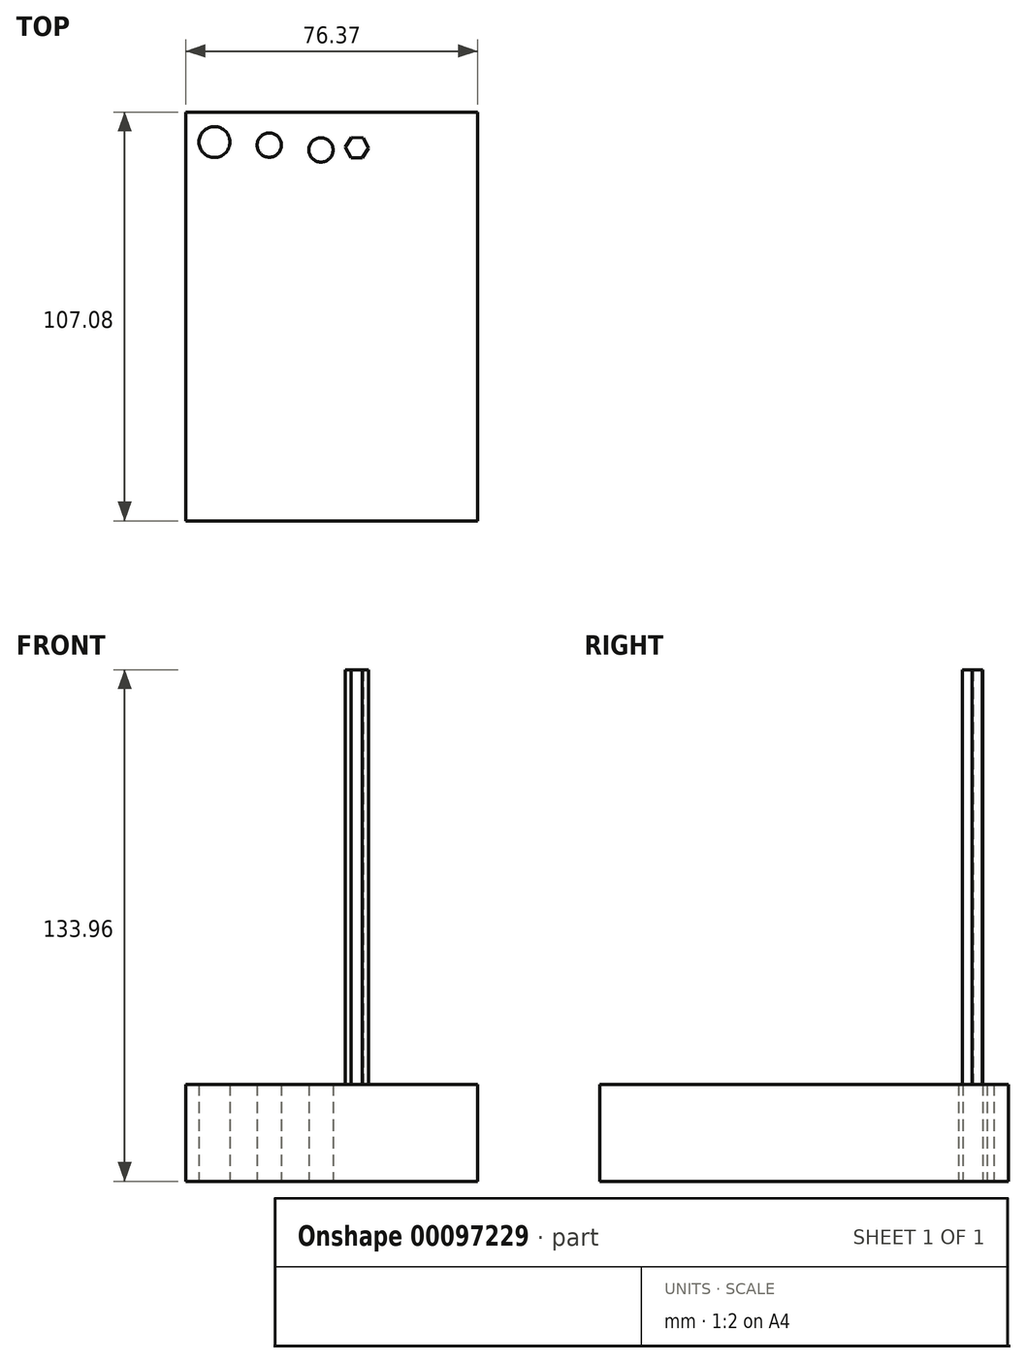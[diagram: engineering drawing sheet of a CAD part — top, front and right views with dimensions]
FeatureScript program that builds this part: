
annotation { "Feature Type Name" : "Feature", "Feature Type Description" : "" }
export const myFeature = defineFeature(function(context is Context, id is Id, definition is map)
    precondition{}
    {
        {
            var Q0;
            Q0=qCreatedBy(makeId("Top.planeOp"),FACE);
            var sketch = newSketch(context, id + "F0", { "sketchPlane" : qUnion([Q0])});
            skLineSegment(sketch, "E0.bottom", {"start": v(-56.88, 53.44) * mm, "end": v(19.49, 53.44) * mm});
            skLineSegment(sketch, "E0.top", {"start": v(-56.88, -53.64) * mm, "end": v(19.49, -53.64) * mm});
            skLineSegment(sketch, "E0.left", {"start": v(-56.88, 53.44) * mm, "end": v(-56.88, -53.64) * mm});
            skLineSegment(sketch, "E0.right", {"start": v(19.49, 53.44) * mm, "end": v(19.49, -53.64) * mm});
            skCircle(sketch, "E1", {"center": v(-49.4, 45.57) * mm, "radius": 4.05 * mm});
            skSolve(sketch);
        }
        {
            var Q0;
            Q0=makeQuery(id+"F0.imprint","IMPRINT",FACE,{"disambiguationData":[TD([[makeQuery(id+"F0.imprint","IMPRINT",EDGE,{"derivedFrom":sQuery(id+"F0.wireOp",EDGE,"E0.bottom")}),-1.0]])]});
            extrude(context, id + "F1", {"entities" : qUnion([Q0]), "depth" : 25.4 * mm});
        }
        {
            var Q0;
            Q0=qCreatedBy(makeId("Top.planeOp"),FACE);
            var sketch = newSketch(context, id + "F2", { "sketchPlane" : qUnion([Q0])});
            skCircle(sketch, "E2", {"center": v(-35.04, 44.78) * mm, "radius": 3.8 * mm});
            skSolve(sketch);
        }
        {
            var Q0;
            Q0=sQuery(id+"F2.wireOp",VERTEX,"E2.center");
            var Q1;
            Q1=makeQuery(id+"F1.opExtrude","SWEPT_BODY",BODY,{"disambiguationData":[OSD([sQuery(id+"F0.wireOp",EDGE,"E0.bottom"),sQuery(id+"F0.wireOp",EDGE,"E0.top"),sQuery(id+"F0.wireOp",EDGE,"E0.left"),sQuery(id+"F0.wireOp",EDGE,"E0.right"),sQuery(id+"F0.wireOp",EDGE,"E1")])]});
            hole(context, id + "F3", {"style" : HoleStyle.SIMPLE, "endStyle" : HoleEndStyle.THROUGH, "oppositeDirection" : true, "holeDiameter" : 6.35 * mm, "locations" : qUnion([Q0]), "scope" : qUnion([Q1]), "isTappedThrough" : true});
        }
        {
            var Q0;
            Q0=qCreatedBy(makeId("Top.planeOp"),FACE);
            var sketch = newSketch(context, id + "F4", { "sketchPlane" : qUnion([Q0])});
            skCircle(sketch, "E3.cCircle", {"center": v(-22.06, 45.19) * mm, "radius": 3.34 * mm, "construction": true});
            skLineSegment(sketch, "E3.0", {"start": v(-20.13, 41.85) * mm, "end": v(-23.99, 41.85) * mm});
            skLineSegment(sketch, "E3.1", {"start": v(-23.99, 41.85) * mm, "end": v(-25.91, 45.19) * mm});
            skLineSegment(sketch, "E3.2", {"start": v(-25.91, 45.19) * mm, "end": v(-23.99, 48.53) * mm});
            skLineSegment(sketch, "E3.3", {"start": v(-23.99, 48.53) * mm, "end": v(-20.13, 48.53) * mm});
            skLineSegment(sketch, "E3.4", {"start": v(-20.13, 48.53) * mm, "end": v(-18.2, 45.19) * mm});
            skLineSegment(sketch, "E3.5", {"start": v(-18.2, 45.19) * mm, "end": v(-20.13, 41.85) * mm});
            skPoint(sketch, "E3.0.midPoint", {"position": v(-22.06, 41.85) * mm});
            skSolve(sketch);
        }
        {
            var Q0;
            Q0 = qSketchRegion(id + "F4", true);
            extrude(context, id + "F5", {"entities" : qUnion([Q0]), "operationType" : NewBodyOperationType.ADD, "depth" : 25.4 * mm});
        }
        {
            var Q0;
            Q0=qCreatedBy(makeId("Top.planeOp"),FACE);
            var sketch = newSketch(context, id + "F6", { "sketchPlane" : qUnion([Q0])});
            skCircle(sketch, "E4.cCircle", {"center": v(-21.5, 43.52) * mm, "radius": 2.87 * mm, "construction": true});
            skLineSegment(sketch, "E4.0", {"start": v(-18.2, 43.57) * mm, "end": v(-19.8, 40.68) * mm});
            skLineSegment(sketch, "E4.1", {"start": v(-19.8, 40.68) * mm, "end": v(-23.1, 40.63) * mm});
            skLineSegment(sketch, "E4.2", {"start": v(-23.1, 40.63) * mm, "end": v(-24.8, 43.46) * mm});
            skLineSegment(sketch, "E4.3", {"start": v(-24.8, 43.46) * mm, "end": v(-23.2, 46.36) * mm});
            skLineSegment(sketch, "E4.4", {"start": v(-23.2, 46.36) * mm, "end": v(-19.9, 46.41) * mm});
            skLineSegment(sketch, "E4.5", {"start": v(-19.9, 46.41) * mm, "end": v(-18.2, 43.57) * mm});
            skPoint(sketch, "E4.0.midPoint", {"position": v(-19, 42.13) * mm});
            skSolve(sketch);
        }
        {
            var Q0;
            Q0=sQuery(id+"F6.wireOp",VERTEX,"E4.cCircle.center");
            var Q1;
            Q1=makeQuery(id+"F1.opExtrude","SWEPT_BODY",BODY,{"disambiguationData":[OSD([sQuery(id+"F0.wireOp",EDGE,"E0.bottom"),sQuery(id+"F0.wireOp",EDGE,"E0.top"),sQuery(id+"F0.wireOp",EDGE,"E0.left"),sQuery(id+"F0.wireOp",EDGE,"E0.right"),sQuery(id+"F0.wireOp",EDGE,"E1")])]});
            hole(context, id + "F7", {"style" : HoleStyle.SIMPLE, "endStyle" : HoleEndStyle.THROUGH, "oppositeDirection" : true, "holeDiameter" : 6.35 * mm, "locations" : qUnion([Q0]), "scope" : qUnion([Q1]), "isTappedThrough" : true});
        }
        {
            var Q0;
            Q0=qCreatedBy(makeId("Top.planeOp"),FACE);
            var sketch = newSketch(context, id + "F8", { "sketchPlane" : qUnion([Q0])});
            skCircle(sketch, "E5.cCircle", {"center": v(-10.65, 47.14) * mm, "radius": 2.78 * mm, "construction": true});
            skLineSegment(sketch, "E5.0", {"start": v(-9.04, 44.35) * mm, "end": v(-12.25, 44.35) * mm});
            skLineSegment(sketch, "E5.1", {"start": v(-12.25, 44.35) * mm, "end": v(-13.86, 47.14) * mm});
            skLineSegment(sketch, "E5.2", {"start": v(-13.86, 47.14) * mm, "end": v(-12.25, 49.92) * mm});
            skLineSegment(sketch, "E5.3", {"start": v(-12.25, 49.92) * mm, "end": v(-9.04, 49.92) * mm});
            skLineSegment(sketch, "E5.4", {"start": v(-9.04, 49.92) * mm, "end": v(-7.43, 47.14) * mm});
            skLineSegment(sketch, "E5.5", {"start": v(-7.43, 47.14) * mm, "end": v(-9.04, 44.35) * mm});
            skPoint(sketch, "E5.0.midPoint", {"position": v(-10.65, 44.35) * mm});
            skSolve(sketch);
        }
        {
            var Q0;
            Q0 = qSketchRegion(id + "F8", true);
            extrude(context, id + "F9", {"entities" : qUnion([Q0]), "operationType" : NewBodyOperationType.ADD, "depth" : 25.4 * mm});
        }
        {
            var Q0;
            Q0=qCreatedBy(makeId("Top.planeOp"),FACE);
            var sketch = newSketch(context, id + "F10", { "sketchPlane" : qUnion([Q0])});
            skCircle(sketch, "E6.cCircle", {"center": v(-11.76, 43.24) * mm, "radius": 3.11 * mm, "construction": true});
            skLineSegment(sketch, "E6.0", {"start": v(-8.17, 43.45) * mm, "end": v(-9.78, 40.24) * mm});
            skLineSegment(sketch, "E6.1", {"start": v(-9.78, 40.24) * mm, "end": v(-13.37, 40.03) * mm});
            skLineSegment(sketch, "E6.2", {"start": v(-13.37, 40.03) * mm, "end": v(-15.35, 43.02) * mm});
            skLineSegment(sketch, "E6.3", {"start": v(-15.35, 43.02) * mm, "end": v(-13.74, 46.24) * mm});
            skLineSegment(sketch, "E6.4", {"start": v(-13.74, 46.24) * mm, "end": v(-10.15, 46.45) * mm});
            skLineSegment(sketch, "E6.5", {"start": v(-10.15, 46.45) * mm, "end": v(-8.17, 43.45) * mm});
            skPoint(sketch, "E6.0.midPoint", {"position": v(-8.98, 41.85) * mm});
            skSolve(sketch);
        }
        {
            var Q0;
            Q0 = qSketchRegion(id + "F10", true);
            extrude(context, id + "F11", {"entities" : qUnion([Q0]), "operationType" : NewBodyOperationType.REMOVE, "oppositeDirection" : true, "depth" : 25.4 * mm});
        }
        {
            var Q0;
            Q0=qCreatedBy(makeId("Top.planeOp"),FACE);
            var sketch = newSketch(context, id + "F12", { "sketchPlane" : qUnion([Q0])});
            skCircle(sketch, "E7.cCircle", {"center": v(-12.04, 44.07) * mm, "radius": 2.63 * mm, "construction": true});
            skLineSegment(sketch, "E7.0", {"start": v(-9, 43.97) * mm, "end": v(-10.61, 41.4) * mm});
            skLineSegment(sketch, "E7.1", {"start": v(-10.61, 41.4) * mm, "end": v(-13.64, 41.5) * mm});
            skLineSegment(sketch, "E7.2", {"start": v(-13.64, 41.5) * mm, "end": v(-15.07, 44.18) * mm});
            skLineSegment(sketch, "E7.3", {"start": v(-15.07, 44.18) * mm, "end": v(-13.46, 46.75) * mm});
            skLineSegment(sketch, "E7.4", {"start": v(-13.46, 46.75) * mm, "end": v(-10.43, 46.65) * mm});
            skLineSegment(sketch, "E7.5", {"start": v(-10.43, 46.65) * mm, "end": v(-9, 43.97) * mm});
            skPoint(sketch, "E7.0.midPoint", {"position": v(-9.81, 42.68) * mm});
            skSolve(sketch);
        }
        {
            var Q0;
            Q0 = qSketchRegion(id + "F12", true);
            extrude(context, id + "F13", {"entities" : qUnion([Q0]), "operationType" : NewBodyOperationType.ADD, "endBound" : BoundingType.THROUGH_ALL, "depth" : 25.4 * mm});
        }
    });
